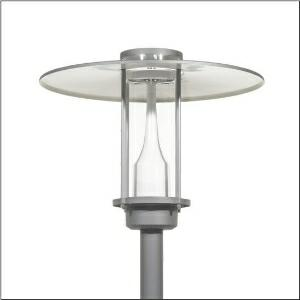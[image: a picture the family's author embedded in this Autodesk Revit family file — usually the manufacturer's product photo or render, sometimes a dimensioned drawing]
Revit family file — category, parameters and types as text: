
# Revit family: city-light_plus_iq___st1_2a_5xa5275mf14hp_2b63
name_source: partatom
category: Lighting Fixtures
units: mm (PartAtom-declared; Revit-internal decimal feet)

## family parameters
Cut with Voids When Loaded = No
Host = Face
Light Source = No
Part Type = Normal
Room Calculation Point = No
Round Connector Dimension = Use Diameter
Shared = No

## types (1)
- --- (1 x LED, 4040 lm, 33.6 W, 2700K)
    Apparent Load = 34 VA
    CIE Flux Codes = 22 60 93 97 100
    Color Rendering = 70
    Color Temperature = 2700K
    Default Elevation = 1800 mm
    Description = City-Light Plus iQ, mast luminaire, Module 540 iQ-SR, primary light control with 3 zone facetted reflector, of plastic, silver coated, highly specular, structured, primary optical cover: cover, of PMMA, transparent, light distribution: ST1.2a, light emission: direct distribution, primary light characteristic: asymmetric, installation type: post-top, LED, High Power LED, rated luminous flux: 4.040lm, luminous efficacy: 120lm/W, light colour: 727, colour temperature: 2700K, control gear: iQ Street-Remote, control: pre-setting: logarithmic dimming characteristic, Street-Remote, Auto-Match, Temp-Guard, Lumen-Switch, Night-Set, Smart-Wire, Light-Fading, Desk-Remote (wireless, voltage-free reading and setting of iQ features in the workshop via application-optimized NFC function/RFID function), optimised constant luminous flux control (CLO 2.0), with terminal, 6-pole, max. 2.5mm², mains connection: 230..240V, AC, 50/60Hz, start of lifetime: 34W, end of service life: 36W, reduction: 15W, luminaire housing, upper part, of glass-fibre reinforced polyester, coated, Siteco® metallic grey (DB 702S), diameter: 750mm, height: 590mm, spigot size: d x l = 76 x 70mm (post-top) | with reducer (optional accessory) 60 x 70mm, mounting height: 3..5m, post-top mast mounting element, of diecast aluminium, coated, Siteco® metallic grey (DB 702S), Module 540 iQ-SR, traffic white (RAL 9016), equipment: Power, protection rating (complete): IP65, insulation class (complete): insulation class II (safety insulation), certification: CE, ENEC, VDE, packaging unit: 1 piece

Light Distribution: ST1.2a
    Height = 590 mm
    Lamp = 1 x LED
    Lamp Light Flux = 4040 lm
    Lamp Power = 33.6 W
    Lamp count = 1
    Length = 750 mm
    Luminous efficacy = 120 lm/W
    Manufacturer = Siteco
    ModVariant = No
    Model = 5XA5275MF14HP
    Number of Poles = 1
    OnlyDefault = Yes
    Power Factor = 1
    Product Name = City-Light Plus iQ | ST1.2a
    Product group = mast luminaire | pylon top
    ProductGroupID = 6100
    Protection Class = Protection class II
    Protection Degree = IP 65
    RLX_Detail_Level = 1
    RLX_Emergency_Light_Flux = 0 lm
    RLX_Emergency_Type = 0
    RLX_Emergency_Type_DB = No
    RlxData = <blob elided: 52557 chars, md5=fe2378db>
    Socket = socket
    Standby Power = 0 W
    System Light Flux = 4040 lm
    System Power = 34 W
    Type Comments = factory setting: luminous flux: 100 % | dim-lin: 254 | 695 mA
    Type Image = l_1006456.jpg
    URL = http://relux.com
    VarID = @adj_152337
    Voltage = 0 V
    Weight = 0.00 kg
    Width = 0 mm  [stored 0 ft]

note: [stored X ft] marks values corroborated as IEEE doubles in the binary element streams (Revit-internal decimal feet)

## geometry (parser evidence)
native form markers: Blend x4, Sweep x13
no freeform markers — native parametric forms only
